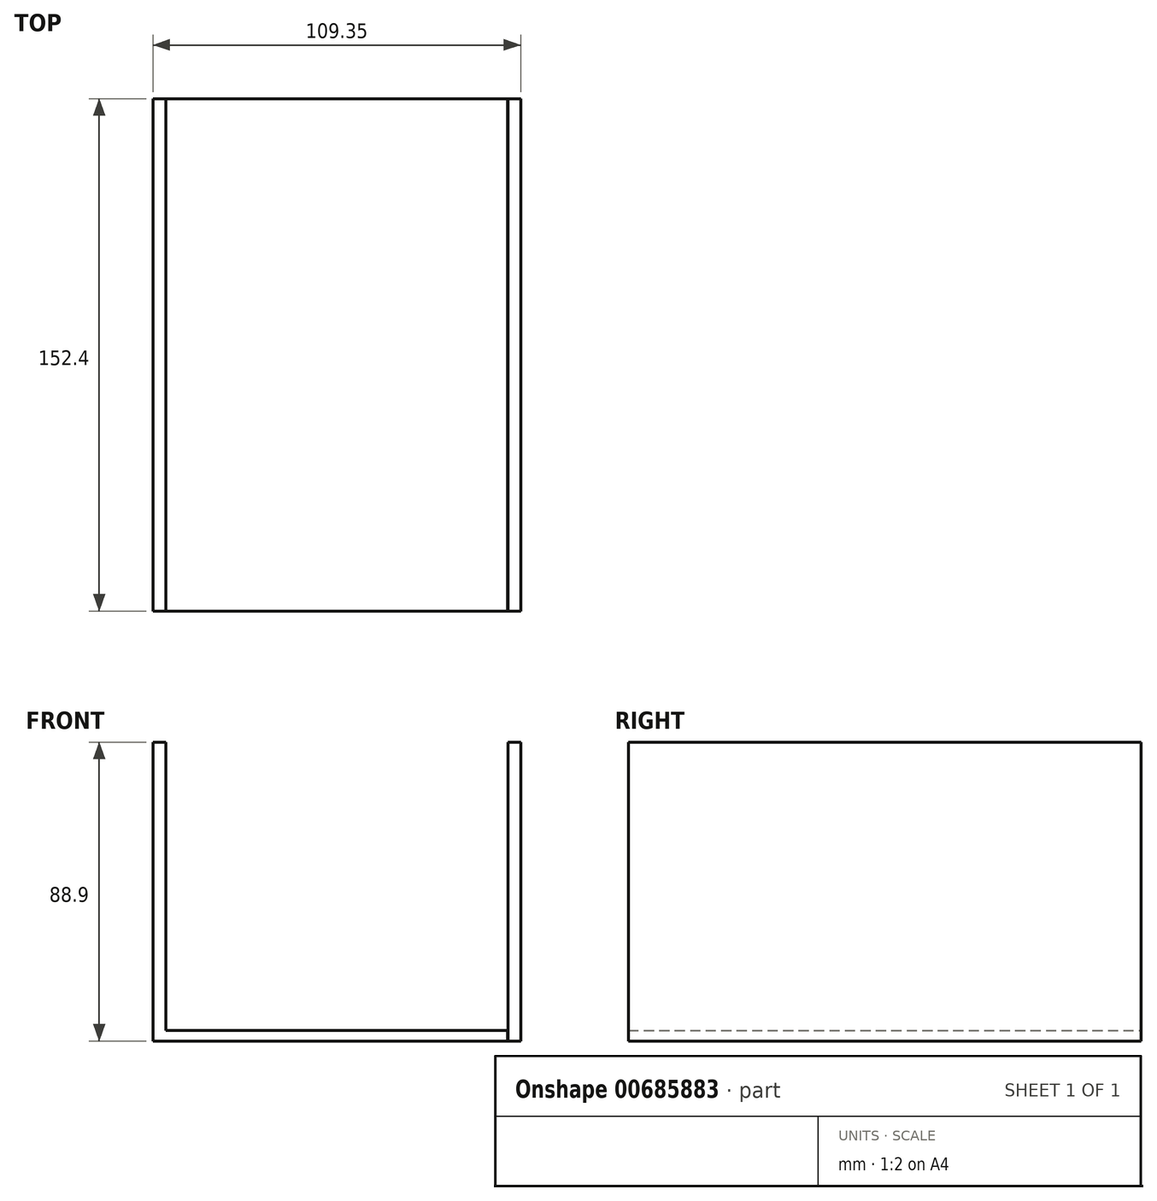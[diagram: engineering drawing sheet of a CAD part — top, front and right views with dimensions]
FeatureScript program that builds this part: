
annotation { "Feature Type Name" : "Feature", "Feature Type Description" : "" }
export const myFeature = defineFeature(function(context is Context, id is Id, definition is map)
    precondition{}
    {
        {
            var Q0;
            Q0=qCreatedBy(makeId("Front.planeOp"),FACE);
            var sketch = newSketch(context, id + "F0", { "sketchPlane" : qUnion([Q0])});
            skLineSegment(sketch, "E0.bottom", {"start": v(-54.6, 44.45) * mm, "end": v(-50.8, 44.45) * mm});
            skLineSegment(sketch, "E0.top", {"start": v(-54.61, -44.45) * mm, "end": v(-50.8, -44.45) * mm});
            skLineSegment(sketch, "E0.left", {"start": v(-54.6, 44.45) * mm, "end": v(-54.61, -44.45) * mm});
            skLineSegment(sketch, "E0.right", {"start": v(-50.8, 44.45) * mm, "end": v(-50.8, -44.45) * mm});
            skPoint(sketch, "E0.middle", {"position": v(-52.7, 0) * mm});
            skLineSegment(sketch, "E1.bottom", {"start": v(-50.8, -44.45) * mm, "end": v(50.8, -44.45) * mm});
            skLineSegment(sketch, "E1.top", {"start": v(-50.8, -41.36) * mm, "end": v(50.8, -41.36) * mm});
            skLineSegment(sketch, "E1.left", {"start": v(-50.8, -44.45) * mm, "end": v(-50.8, -41.36) * mm});
            skLineSegment(sketch, "E1.right", {"start": v(50.8, -44.45) * mm, "end": v(50.8, -41.36) * mm});
            skPoint(sketch, "E1.middle", {"position": v(0, -42.9) * mm});
            skLineSegment(sketch, "E2.bottom", {"start": v(50.93, 44.45) * mm, "end": v(54.74, 44.45) * mm});
            skLineSegment(sketch, "E2.top", {"start": v(50.93, -44.45) * mm, "end": v(54.74, -44.45) * mm});
            skLineSegment(sketch, "E2.left", {"start": v(50.93, 44.45) * mm, "end": v(50.93, -44.45) * mm});
            skLineSegment(sketch, "E2.right", {"start": v(54.74, 44.45) * mm, "end": v(54.74, -44.45) * mm});
            skPoint(sketch, "E2.middle", {"position": v(52.83, 0) * mm});
            skSolve(sketch);
        }
        {
            var Q0;
            Q0=makeQuery(id+"F0.imprint","IMPRINT",FACE,{"disambiguationData":[TD([[makeQuery(id+"F0.imprint","IMPRINT",EDGE,{"derivedFrom":sQuery(id+"F0.wireOp",EDGE,"E0.bottom")}),-1.0]])]});
            var Q1;
            Q1=makeQuery(id+"F0.imprint","IMPRINT",FACE,{"disambiguationData":[TD([[makeQuery(id+"F0.imprint","IMPRINT",EDGE,{"derivedFrom":sQuery(id+"F0.wireOp",EDGE,"E2.bottom")}),-1.0]])]});
            var Q2;
            Q2=makeQuery(id+"F0.imprint","IMPRINT",FACE,{"disambiguationData":[TD([[makeQuery(id+"F0.imprint","IMPRINT",EDGE,{"derivedFrom":sQuery(id+"F0.wireOp",EDGE,"E1.bottom")}),1.0]])]});
            extrude(context, id + "F1", {"entities" : qUnion([Q0, Q1, Q2]), "endBound" : BoundingType.SYMMETRIC, "depth" : 152.4 * mm, "offsetDistance" : 25.4 * mm});
        }
    });
